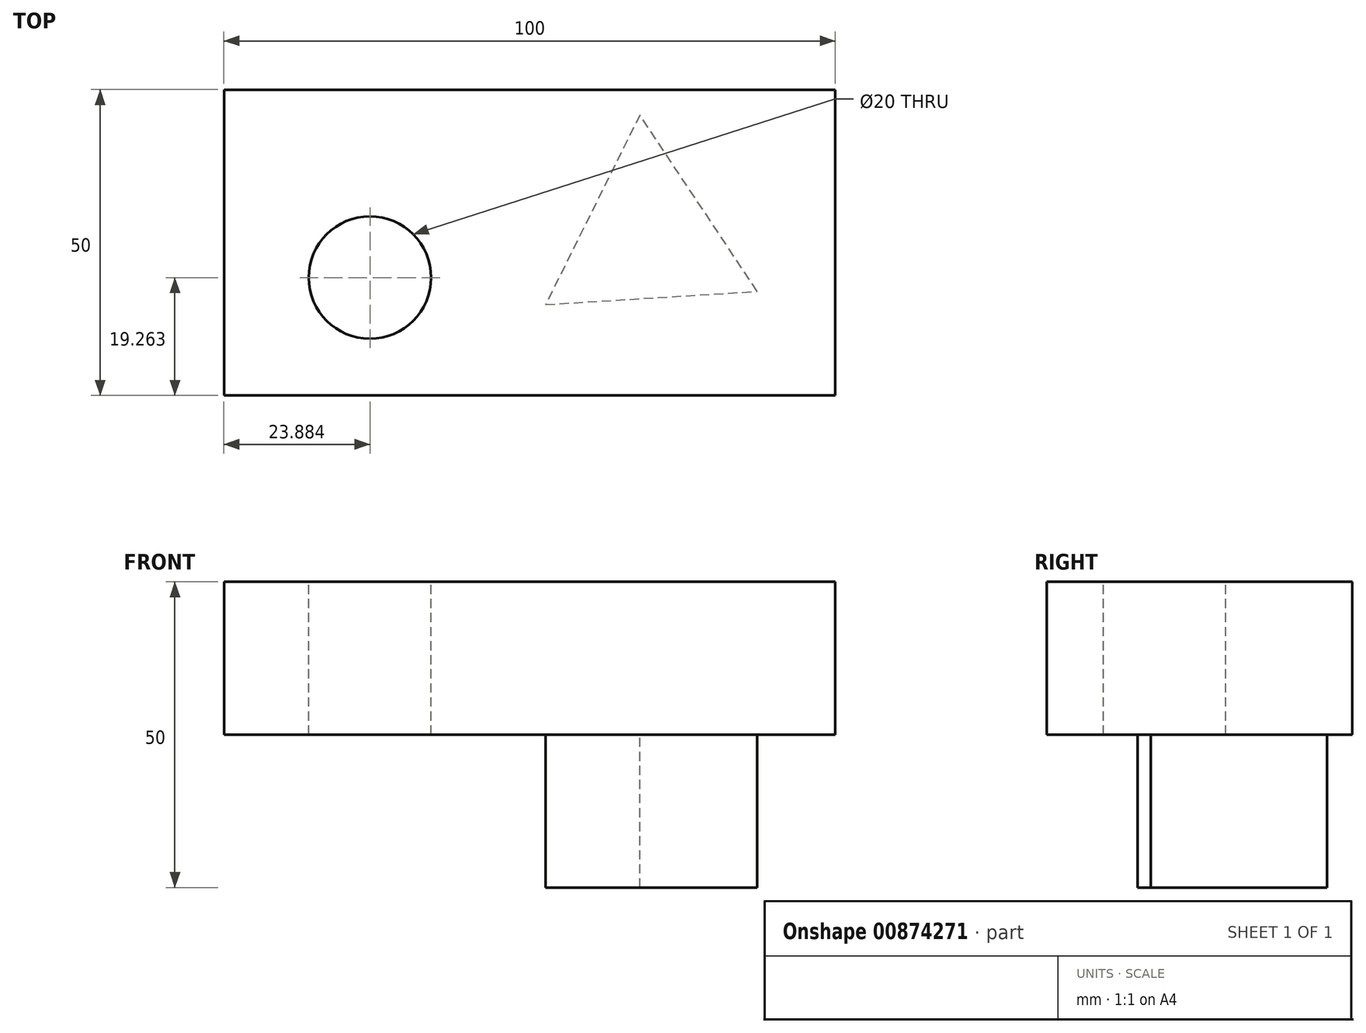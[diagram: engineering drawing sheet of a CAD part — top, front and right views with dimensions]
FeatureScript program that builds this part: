
annotation { "Feature Type Name" : "Feature", "Feature Type Description" : "" }
export const myFeature = defineFeature(function(context is Context, id is Id, definition is map)
    precondition{}
    {
        {
            var Q0;
            Q0=qCreatedBy(makeId("Top.planeOp"),FACE);
            var sketch = newSketch(context, id + "F0", { "sketchPlane" : qUnion([Q0])});
            skLineSegment(sketch, "E0.bottom", {"start": v(-7.29, 33.08) * mm, "end": v(92.71, 33.08) * mm});
            skLineSegment(sketch, "E0.top", {"start": v(-7.29, 83.08) * mm, "end": v(92.71, 83.08) * mm});
            skLineSegment(sketch, "E0.left", {"start": v(-7.29, 33.08) * mm, "end": v(-7.29, 83.08) * mm});
            skLineSegment(sketch, "E0.right", {"start": v(92.71, 33.08) * mm, "end": v(92.71, 83.08) * mm});
            skSolve(sketch);
        }
        {
            var Q0;
            Q0 = qSketchRegion(id + "F0", true);
            extrude(context, id + "F1", {"entities" : qUnion([Q0]), "depth" : 25 * mm, "offsetDistance" : 25 * mm});
        }
        {
            var Q0;
            Q0=makeQuery(id+"F1.opExtrude","CAP_FACE",FACE,{"disambiguationData":[OSD([sQuery(id+"F0.wireOp",EDGE,"E0.bottom"),sQuery(id+"F0.wireOp",EDGE,"E0.top"),sQuery(id+"F0.wireOp",EDGE,"E0.left"),sQuery(id+"F0.wireOp",EDGE,"E0.right")])],"isStart":false});
            var sketch = newSketch(context, id + "F2", { "sketchPlane" : qUnion([Q0])});
            skCircle(sketch, "E1", {"center": v(16.6, 52.34) * mm, "radius": 10 * mm});
            skSolve(sketch);
        }
        {
            var Q0;
            Q0 = qSketchRegion(id + "F2", true);
            extrude(context, id + "F3", {"entities" : qUnion([Q0]), "operationType" : NewBodyOperationType.REMOVE, "endBound" : BoundingType.THROUGH_ALL, "oppositeDirection" : true, "depth" : 25 * mm, "offsetDistance" : 25 * mm});
        }
        {
            var Q0;
            Q0=makeQuery(id+"F1.opExtrude","CAP_FACE",FACE,{"disambiguationData":[OSD([sQuery(id+"F0.wireOp",EDGE,"E0.bottom"),sQuery(id+"F0.wireOp",EDGE,"E0.top"),sQuery(id+"F0.wireOp",EDGE,"E0.left"),sQuery(id+"F0.wireOp",EDGE,"E0.right")])],"isStart":true});
            var sketch = newSketch(context, id + "F4", { "sketchPlane" : qUnion([Q0])});
            skCircle(sketch, "E2.cCircle", {"center": v(62, -58.99) * mm, "radius": 10 * mm, "construction": true});
            skLineSegment(sketch, "E2.0", {"start": v(60.76, -78.95) * mm, "end": v(45.34, -47.93) * mm});
            skLineSegment(sketch, "E2.1", {"start": v(45.34, -47.93) * mm, "end": v(79.91, -50.08) * mm});
            skLineSegment(sketch, "E2.2", {"start": v(79.91, -50.08) * mm, "end": v(60.76, -78.95) * mm});
            skPoint(sketch, "E2.0.midPoint", {"position": v(53.05, -63.44) * mm});
            skSolve(sketch);
        }
        {
            var Q0;
            Q0 = qSketchRegion(id + "F4", true);
            extrude(context, id + "F5", {"entities" : qUnion([Q0]), "operationType" : NewBodyOperationType.ADD, "depth" : 25 * mm, "offsetDistance" : 25 * mm});
        }
    });
